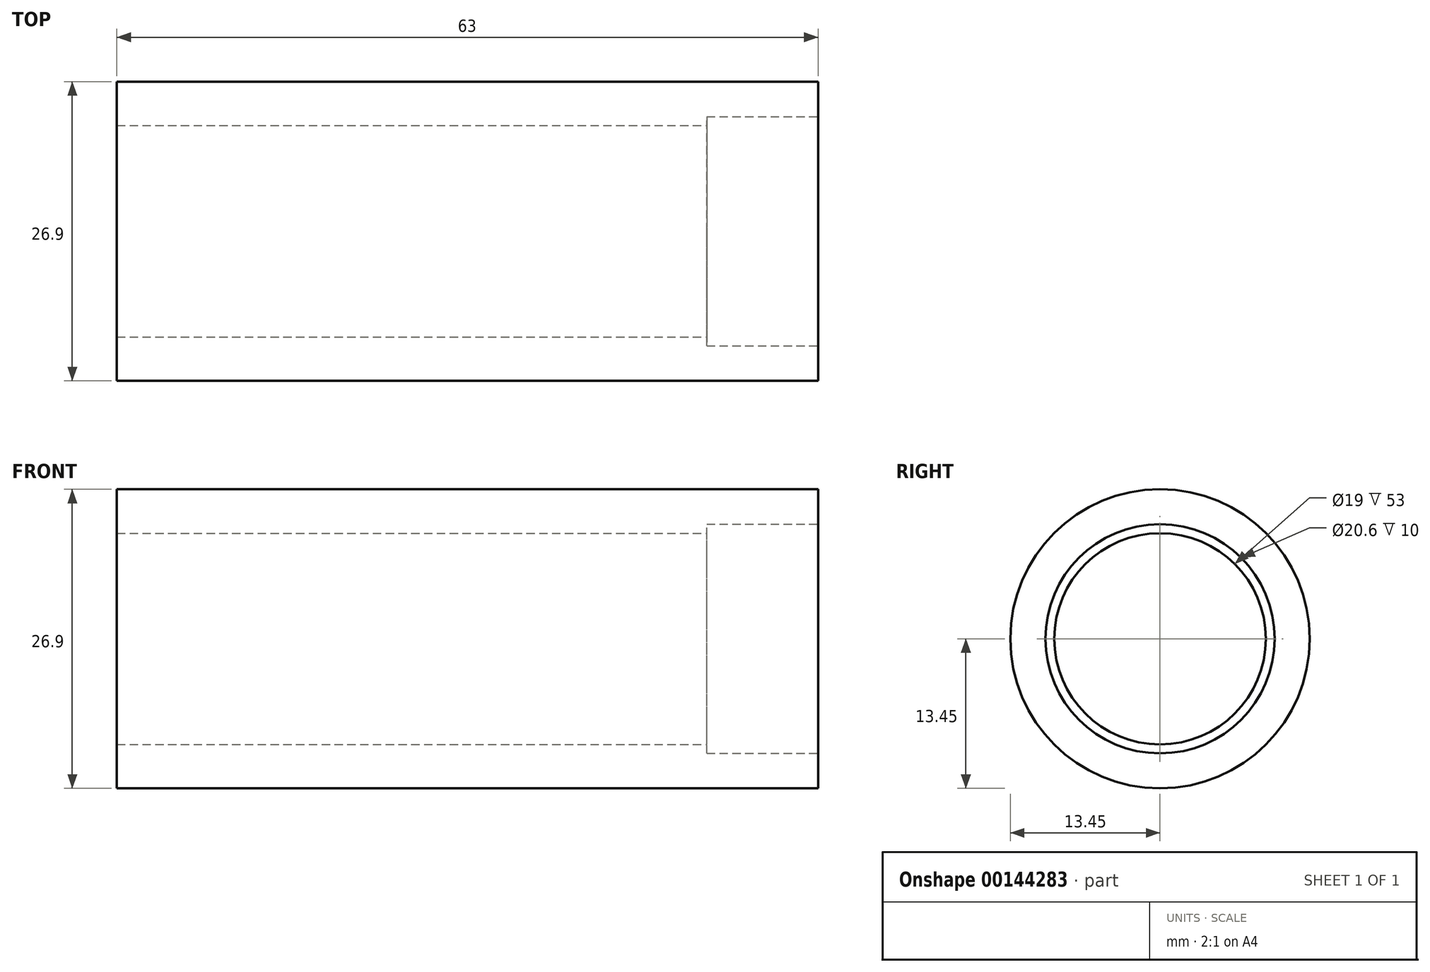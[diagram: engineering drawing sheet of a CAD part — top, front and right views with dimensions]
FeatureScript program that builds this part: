
annotation { "Feature Type Name" : "Feature", "Feature Type Description" : "" }
export const myFeature = defineFeature(function(context is Context, id is Id, definition is map)
    precondition{}
    {
        {
            var Q0;
            Q0=qCreatedBy(makeId("Right.planeOp"),FACE);
            var sketch = newSketch(context, id + "F0", { "sketchPlane" : qUnion([Q0])});
            skCircle(sketch, "E0", {"center": v(0, 0) * mm, "radius": 13.45 * mm});
            skSolve(sketch);
        }
        {
            var Q0;
            Q0 = qSketchRegion(id + "F0", true);
            extrude(context, id + "F1", {"entities" : qUnion([Q0]), "depth" : 63 * mm});
        }
        {
            var Q0;
            Q0=makeQuery(id+"F1.opExtrude","CAP_FACE",FACE,{"disambiguationData":[OSD([sQuery(id+"F0.wireOp",EDGE,"E0")])],"isStart":false});
            var sketch = newSketch(context, id + "F2", { "sketchPlane" : qUnion([Q0])});
            skCircle(sketch, "E1", {"center": v(0, 0) * mm, "radius": 9.5 * mm});
            skSolve(sketch);
        }
        {
            var Q0;
            Q0 = qSketchRegion(id + "F2", true);
            extrude(context, id + "F3", {"entities" : qUnion([Q0]), "operationType" : NewBodyOperationType.REMOVE, "endBound" : BoundingType.THROUGH_ALL, "oppositeDirection" : true, "depth" : 25 * mm});
        }
        {
            var Q0;
            Q0=makeQuery(id+"F1.opExtrude","CAP_FACE",FACE,{"disambiguationData":[OSD([sQuery(id+"F0.wireOp",EDGE,"E0")])],"isStart":false});
            var sketch = newSketch(context, id + "F4", { "sketchPlane" : qUnion([Q0])});
            skCircle(sketch, "E2", {"center": v(0, 0) * mm, "radius": 10.3 * mm});
            skSolve(sketch);
        }
        {
            var Q0;
            Q0 = qSketchRegion(id + "F4", true);
            extrude(context, id + "F5", {"entities" : qUnion([Q0]), "operationType" : NewBodyOperationType.REMOVE, "oppositeDirection" : true, "depth" : 10 * mm});
        }
    });
